FREECAD ASSEMBLY — COMPONENT RECIPES ("legs")

This assembly document has 15 components, labeled P0..P14 below (a component is one placed body or linked part). 15 of them carry a construction recipe — the FreeCAD feature program that regenerates the part from scratch, quoted from this document or its linked companion documents; the rest are supplied as boundary geometry only. No exploded tour is included for this assembly.
COMPONENT P0 — recipe-attached ("steel-profile-40x40x400", a linked part whose construction recipe lives in a companion FreeCAD document of the same project; that document's serialized recipe follows).
Construction recipe (the companion document, serialized — sketch geometry with constraints, then the solid features built on it; lengths are millimeters unless a unit is written):

FCSTD DOCUMENT  (FreeCAD 1.0R39319 (Git))
Label: steel-profile-40x40x400
License: All rights reserved
LicenseURL: http://en.wikipedia.org/wiki/All_rights_reserved
objects: Sketcher::SketchObject×1, PartDesign::Pad×1, PartDesign::Body×1, App::Part×1
note: 6 computed .brp shape members not serialized (recipe doc carries the construction recipe); baked Part::Feature solids carry a one-line shape summary decoded from their .brp

FEATURE [Sketcher::SketchObject] Sketch
  ArcFitTolerance = 1e-06
  AttachmentSupport = -> [XY_Plane001]
  FullyConstrained = true
  MakeInternals = false
  MapMode = 5
  sketch-geometry (18):
    g0: LineSegment StartX=2 StartY=-9e-16 StartZ=0 EndX=38 EndY=-9e-16 EndZ=0
    g1: LineSegment StartX=40 StartY=2 StartZ=0 EndX=40 EndY=38 EndZ=0
    g2: LineSegment StartX=38 StartY=40 StartZ=0 EndX=2 EndY=40 EndZ=0
    g3: LineSegment StartX=-1.3e-15 StartY=38 StartZ=0 EndX=-1.3e-15 EndY=2 EndZ=0
    g4: ArcOfCircle CenterX=2 CenterY=2 CenterZ=0 NormalX=0 NormalY=0 NormalZ=1 AngleXU=0 Radius=2 StartAngle=3.14159 EndAngle=4.71239
    g5: ArcOfCircle CenterX=38 CenterY=2 CenterZ=0 NormalX=0 NormalY=0 NormalZ=1 AngleXU=0 Radius=2 StartAngle=4.71239 EndAngle=6.28319
    g6: ArcOfCircle CenterX=38 CenterY=38 CenterZ=0 NormalX=0 NormalY=0 NormalZ=1 AngleXU=0 Radius=2 StartAngle=0 EndAngle=1.5708
    g7: ArcOfCircle CenterX=2 CenterY=38 CenterZ=0 NormalX=0 NormalY=0 NormalZ=1 AngleXU=0 Radius=2 StartAngle=1.5708 EndAngle=3.14159
    g8: LineSegment StartX=3 StartY=3 StartZ=0 EndX=37 EndY=3 EndZ=0
    g9: LineSegment StartX=37 StartY=3 StartZ=0 EndX=37 EndY=37 EndZ=0
    g10: LineSegment StartX=37 StartY=37 StartZ=0 EndX=3 EndY=37 EndZ=0
    g11: LineSegment StartX=3 StartY=37 StartZ=0 EndX=3 EndY=3 EndZ=0
    g12: LineSegment [constr] StartX=2 StartY=2 StartZ=0 EndX=3 EndY=3 EndZ=0
    g13: LineSegment [constr] StartX=38 StartY=2 StartZ=0 EndX=37 EndY=3 EndZ=0
    g14: LineSegment [constr] StartX=38 StartY=38 StartZ=0 EndX=37 EndY=37 EndZ=0
    g15: LineSegment [constr] StartX=2 StartY=38 StartZ=0 EndX=3 EndY=37 EndZ=0
    g16: GeomPoint [constr] X=-1.6e-15 Y=-1.1e-15 Z=0
    g17: GeomPoint [constr] X=40 Y=40 Z=0
  constraints (43):
    c: Tangent(g0,g4) = -1.5708
    c: Tangent(g0,g5) = -1.5708
    c: Tangent(g1,g5) = -1.5708
    c: Tangent(g1,g6) = -1.5708
    c: Tangent(g2,g6) = -1.5708
    c: Tangent(g2,g7) = -1.5708
    c: Tangent(g3,g7) = -1.5708
    c: Tangent(g3,g4) = -1.5708
    c: Horizontal(g0)
    c: Horizontal(g2)
    c: Vertical(g1)
    c: Vertical(g3)
    c: Equal(g4,g5)
    c: Equal(g5,g6)
    c: Equal(g6,g7)
    c: Coincident(g8,g9)
    c: Coincident(g9,g10)
    c: Coincident(g10,g11)
    c: Coincident(g11,g8)
    c: Horizontal(g8)
    c: Horizontal(g10)
    c: Vertical(g9)
    c: Vertical(g11)
    c: Coincident(g12,g4)
    c: Coincident(g12,g8)
    c: Coincident(g13,g5)
    c: Coincident(g13,g9)
    c: Coincident(g14,g6)
    c: Coincident(g14,g10)
    c: Coincident(g15,g7)
    c: Coincident(g15,g11)
    c: Perpendicular(g12,g13)
    c: Perpendicular(g13,g14)
    c: Perpendicular(g14,g15)
    c: PointOnObject(g16,g0)
    c: PointOnObject(g16,g3)
    c: PointOnObject(g17,g1)
    c: PointOnObject(g17,g2)
    c: Distance(g1,g3) = 40
    c: Distance(g0,g2) = 40
    c: Radius(g5) = 2
    c: Distance(g8,g0) = 3
    c: Coincident(g16,g-1)
FEATURE [PartDesign::Pad] Pad
  Direction = (0,0,1)
  Length = 400
  Length2 = 10
  Profile = -> Sketch
  ReferenceAxis = -> Sketch [N_Axis]
  Suppressed = false
  Type = 0
FEATURE [PartDesign::Body] Body
  AllowCompound = false
  Group = -> [Sketch,Pad]
  Origin = -> Origin001
  Tip = -> Pad
FEATURE [App::Part] Part  label="steel-profile-40x40x400"
  Group = -> [Body]
  Origin = -> Origin
COMPONENT P1 — same part as P0; its construction recipe is shown at P0.
COMPONENT P2 — same part as P0; its construction recipe is shown at P0.
COMPONENT P3 — same part as P0; its construction recipe is shown at P0.
COMPONENT P4 — same part as P0; its construction recipe is shown at P0.
COMPONENT P5 — same part as P0; its construction recipe is shown at P0.
COMPONENT P6 — same part as P0; its construction recipe is shown at P0.
COMPONENT P7 — same part as P0; its construction recipe is shown at P0.
COMPONENT P8 — same part as P0; its construction recipe is shown at P0.
COMPONENT P9 — same part as P0; its construction recipe is shown at P0.
COMPONENT P10 — same part as P0; its construction recipe is shown at P0.
COMPONENT P11 — same part as P0; its construction recipe is shown at P0.
COMPONENT P12 — same part as P0; its construction recipe is shown at P0.
COMPONENT P13 — same part as P0; its construction recipe is shown at P0.
COMPONENT P14 — recipe-attached ("x-stepper-mounting-profile", a linked part whose construction recipe lives in a companion FreeCAD document of the same project; that document's serialized recipe follows).
Construction recipe (the companion document, serialized — sketch geometry with constraints, then the solid features built on it; lengths are millimeters unless a unit is written):

FCSTD DOCUMENT  (FreeCAD 1.0R39319 (Git))
Label: x-stepper-mounting-profile
License: All rights reserved
LicenseURL: http://en.wikipedia.org/wiki/All_rights_reserved
objects: Sketcher::SketchObject×2, PartDesign::Pad×1, PartDesign::Hole×1, PartDesign::Body×1, App::Part×1
note: 11 computed .brp shape members not serialized (recipe doc carries the construction recipe); baked Part::Feature solids carry a one-line shape summary decoded from their .brp

FEATURE [Sketcher::SketchObject] Sketch
  ArcFitTolerance = 1e-06
  AttachmentSupport = -> [YZ_Plane]
  FullyConstrained = true
  MakeInternals = false
  MapMode = 5
  Placement = pos=(0,0,0) rot=(0.57735,0.57735,0.57735;2.0944rad)
  sketch-geometry (18):
    g0: LineSegment StartX=2 StartY=0 StartZ=0 EndX=38 EndY=0 EndZ=0
    g1: LineSegment StartX=40 StartY=2 StartZ=0 EndX=40 EndY=38 EndZ=0
    g2: LineSegment StartX=38 StartY=40 StartZ=0 EndX=2 EndY=40 EndZ=0
    g3: LineSegment StartX=0 StartY=38 StartZ=0 EndX=0 EndY=2 EndZ=0
    g4: ArcOfCircle CenterX=2 CenterY=2 CenterZ=0 NormalX=0 NormalY=0 NormalZ=1 AngleXU=0 Radius=2 StartAngle=3.14159 EndAngle=4.71239
    g5: ArcOfCircle CenterX=38 CenterY=2 CenterZ=0 NormalX=0 NormalY=0 NormalZ=1 AngleXU=0 Radius=2 StartAngle=4.71239 EndAngle=6.28319
    g6: ArcOfCircle CenterX=38 CenterY=38 CenterZ=0 NormalX=0 NormalY=0 NormalZ=1 AngleXU=0 Radius=2 StartAngle=0 EndAngle=1.5708
    g7: ArcOfCircle CenterX=2 CenterY=38 CenterZ=0 NormalX=0 NormalY=0 NormalZ=1 AngleXU=0 Radius=2 StartAngle=1.5708 EndAngle=3.14159
    g8: LineSegment StartX=3 StartY=3 StartZ=0 EndX=37 EndY=3 EndZ=0
    g9: LineSegment StartX=37 StartY=3 StartZ=0 EndX=37 EndY=37 EndZ=0
    g10: LineSegment StartX=37 StartY=37 StartZ=0 EndX=3 EndY=37 EndZ=0
    g11: LineSegment StartX=3 StartY=37 StartZ=0 EndX=3 EndY=3 EndZ=0
    g12: LineSegment [constr] StartX=2 StartY=2 StartZ=0 EndX=3 EndY=3 EndZ=0
    g13: LineSegment [constr] StartX=38 StartY=2 StartZ=0 EndX=37 EndY=3 EndZ=0
    g14: LineSegment [constr] StartX=38 StartY=38 StartZ=0 EndX=37 EndY=37 EndZ=0
    g15: LineSegment [constr] StartX=2 StartY=38 StartZ=0 EndX=3 EndY=37 EndZ=0
    g16: GeomPoint [constr] X=0 Y=0 Z=0
    g17: GeomPoint [constr] X=40 Y=40 Z=0
  constraints (43):
    c: Tangent(g0,g4) = -1.5708
    c: Tangent(g0,g5) = -1.5708
    c: Tangent(g1,g5) = -1.5708
    c: Tangent(g1,g6) = -1.5708
    c: Tangent(g2,g6) = -1.5708
    c: Tangent(g2,g7) = -1.5708
    c: Tangent(g3,g7) = -1.5708
    c: Tangent(g3,g4) = -1.5708
    c: Horizontal(g0)
    c: Horizontal(g2)
    c: Vertical(g1)
    c: Vertical(g3)
    c: Equal(g4,g5)
    c: Equal(g5,g6)
    c: Equal(g6,g7)
    c: Coincident(g8,g9)
    c: Coincident(g9,g10)
    c: Coincident(g10,g11)
    c: Coincident(g11,g8)
    c: Horizontal(g8)
    c: Horizontal(g10)
    c: Vertical(g9)
    c: Vertical(g11)
    c: Coincident(g12,g4)
    c: Coincident(g12,g8)
    c: Coincident(g13,g5)
    c: Coincident(g13,g9)
    c: Coincident(g14,g6)
    c: Coincident(g14,g10)
    c: Coincident(g15,g7)
    c: Coincident(g15,g11)
    c: Perpendicular(g12,g13)
    c: Perpendicular(g13,g14)
    c: Perpendicular(g14,g15)
    c: PointOnObject(g16,g0)
    c: PointOnObject(g16,g3)
    c: PointOnObject(g17,g1)
    c: PointOnObject(g17,g2)
    c: Distance(g1,g3) = 40
    c: Distance(g0,g2) = 40
    c: Radius(g5) = 2
    c: Distance(g8,g0) = 3
    c: Coincident(g16,g-1)
FEATURE [PartDesign::Pad] Pad
  Direction = (1,0,0)
  Length = 400
  Length2 = 10
  Placement = pos=(0,0,0) rot=(1,1,1;2.0944rad)
  Profile = -> Sketch
  ReferenceAxis = -> Sketch [N_Axis]
  Suppressed = false
  Type = 0
FEATURE [Sketcher::SketchObject] Sketch001
  ArcFitTolerance = 1e-06
  AttachmentSupport = -> [Pad]
  FullyConstrained = false
  MakeInternals = false
  MapMode = 5
  Placement = pos=(0,8.8e-15,40) rot=(0,0,-1;1.5708rad)
  sketch-geometry (5):
    g0: LineSegment [constr] StartX=0 StartY=0 StartZ=0 EndX=0 EndY=400 EndZ=0
    g1: LineSegment [constr] StartX=0 StartY=0 StartZ=0 EndX=-40 EndY=0 EndZ=0
    g2: LineSegment [constr] StartX=0 StartY=200 StartZ=0 EndX=-40 EndY=200 EndZ=0
    g3: Circle CenterX=-20 CenterY=180 CenterZ=0 NormalX=0 NormalY=0 NormalZ=1 AngleXU=0 Radius=2
    g4: Circle CenterX=-20 CenterY=220 CenterZ=0 NormalX=0 NormalY=0 NormalZ=1 AngleXU=0 Radius=2
  constraints (12):
    c: Distance(g0) = 400
    c: Coincident(g0,g-1)
    c: Vertical(g0)
    c: Distance(g1) = 40
    c: Coincident(g1,g0)
    c: PointOnObject(g1,g-1)
    c: Distance(g2) = 40
    c: Symmetric(g0,g0,g2)
    c: Horizontal(g2)
    c: Diameter(g3) = 4
    c: Distance(g3,g2) = 20
    c: Diameter(g4) = 4
FEATURE [PartDesign::Hole] Hole
  BaseFeature = -> Pad
  CustomThreadClearance = 0
  Depth = 25
  DepthType = 0
  Diameter = 3.3
  DrillForDepth = false
  DrillPoint = 1
  DrillPointAngle = 118
  HoleCutCountersinkAngle = 90
  HoleCutCustomValues = false
  HoleCutDepth = 0
  HoleCutDiameter = 6.1
  HoleCutType = 0
  ModelThread = false
  Placement = pos=(0,0,0) rot=(1,1,1;2.0944rad)
  Profile = -> Sketch001
  Suppressed = false
  Tapered = false
  TaperedAngle = 90
  ThreadClass = 0
  ThreadDepth = 25
  ThreadDepthType = 0
  ThreadDirection = 0
  ThreadFit = 0
  ThreadSize = 11
  ThreadType = 1
  Threaded = true
  UseCustomThreadClearance = false
FEATURE [PartDesign::Body] Body
  AllowCompound = false
  Group = -> [Sketch,Pad,Sketch001,Hole]
  Origin = -> Origin
  Tip = -> Hole
FEATURE [App::Part] Part  label="x-stepper-mounting-profile"
  Group = -> [Body]
  Origin = -> Origin001
PROVENANCE & LICENSES
A FreeCAD (.FCStd) document from a public repository crawl; recipes are the document's own serialized feature recipes (and, for linked parts, companion documents' recipes).
License: as declared in the source repository (recorded in the dataset sidecar).
